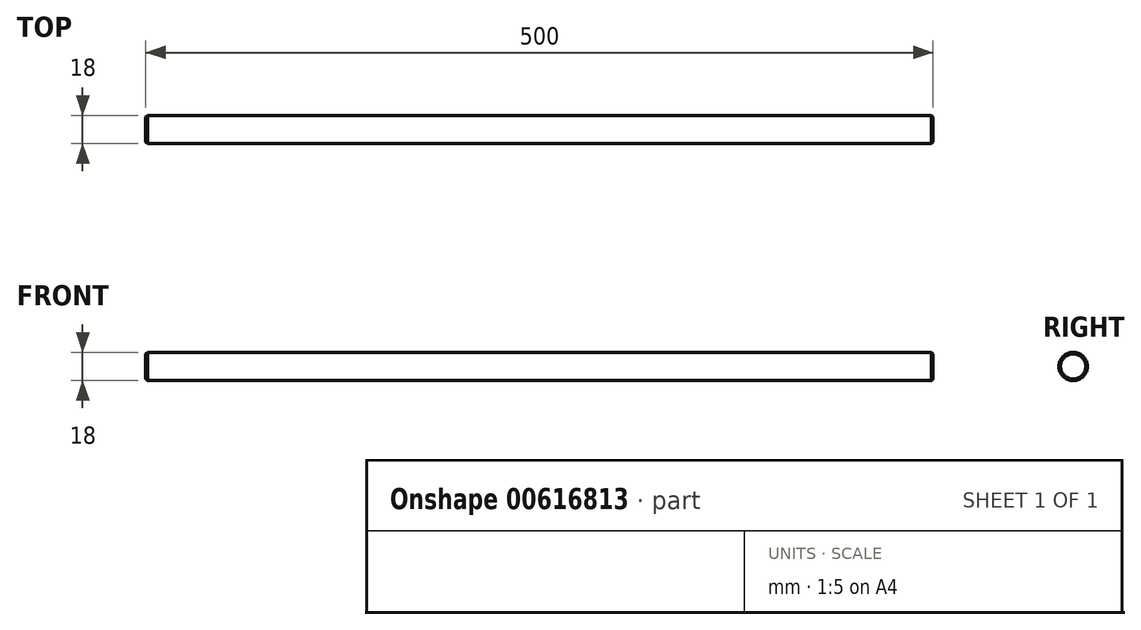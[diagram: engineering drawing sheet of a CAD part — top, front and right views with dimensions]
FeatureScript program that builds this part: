
annotation { "Feature Type Name" : "Feature", "Feature Type Description" : "" }
export const myFeature = defineFeature(function(context is Context, id is Id, definition is map)
    precondition{}
    {
        {
            var Q0;
            Q0=qCreatedBy(makeId("Right.planeOp"),FACE);
            var sketch = newSketch(context, id + "F0", { "sketchPlane" : qUnion([Q0])});
            skCircle(sketch, "E0", {"center": v(0, 0) * mm, "radius": 9 * mm});
            skSolve(sketch);
        }
        {
            var Q0;
            Q0 = qSketchRegion(id + "F0", true);
            extrude(context, id + "F1", {"entities" : qUnion([Q0]), "depth" : 500 * mm, "offsetDistance" : 25 * mm, "symmetric" : true});
        }
        {
            var Q0;
            Q0=makeQuery(id+"F1.opExtrude","CAP_EDGE",EDGE,{"disambiguationData":[OSD([sQuery(id+"F0.wireOp",EDGE,"E0")])],"isStart":true});
            var Q1;
            Q1=makeQuery(id+"F1.opExtrude","CAP_EDGE",EDGE,{"disambiguationData":[OSD([sQuery(id+"F0.wireOp",EDGE,"E0")])],"isStart":false});
            chamfer(context, id + "F2", {"entities" : qUnion([Q0, Q1]), "width" : 1 * mm, "tangentPropagation" : true});
        }
    });
